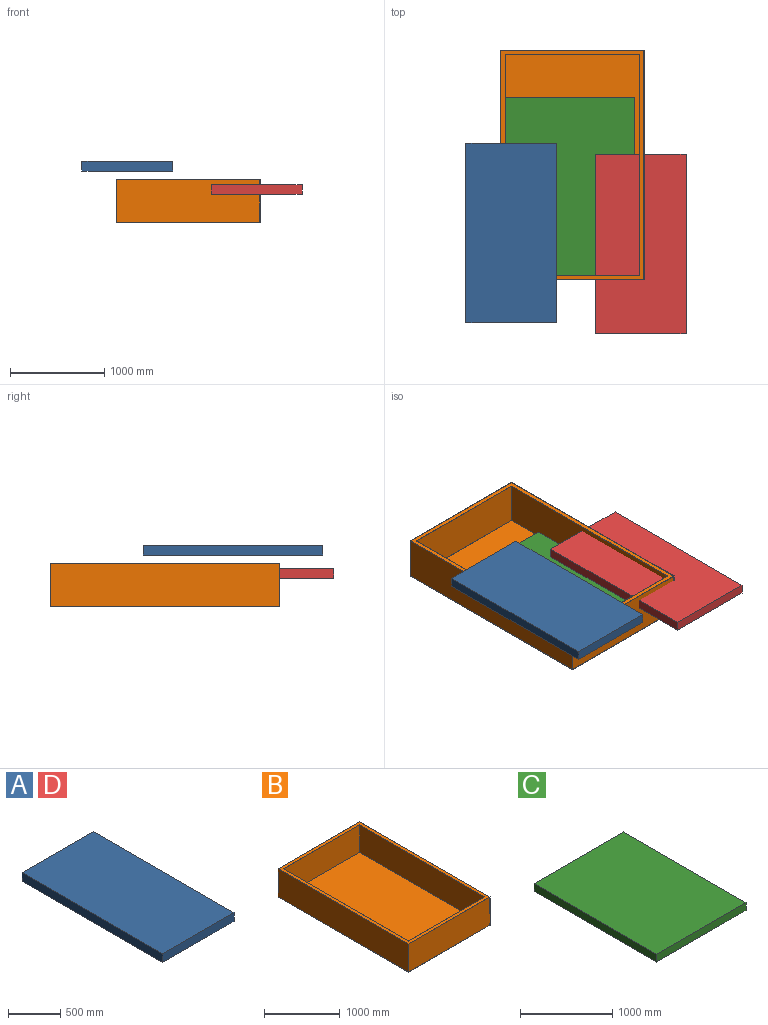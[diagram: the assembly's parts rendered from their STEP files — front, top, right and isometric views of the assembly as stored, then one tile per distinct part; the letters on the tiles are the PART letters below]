
ASSEMBLY  parts=4 mates=3
PART A: 6 faces, bbox 965.2x1905x101.6 mm
  f0: plane 1905x101.6mm, normal (-1,0,0), area 193548mm2, adj f1,f3,f4,f5
  f1: plane 965.2x101.6mm, normal (0,-1,0), area 98064.3mm2, adj f0,f2,f4,f5
  f2: plane 1905x101.6mm, normal (1,0,0), area 193548mm2, adj f1,f3,f4,f5
  f3: plane 965.2x101.6mm, normal (0,1,0), area 98064.3mm2, adj f0,f2,f4,f5
  f4: plane 1905x965.2mm, normal (0,0,1), area 1838706mm2, adj f0,f1,f2,f3
  f5: plane 1905x965.2mm, normal (0,0,-1), area 1838706mm2, adj f0,f1,f2,f3
PART B: 22 faces, bbox 1524x2438.4x457.2 mm
  f0: plane 2438.4x1524mm, normal (0,0,1), area 392257.3mm2, adj f1,f2,f3,f4,f6,f7,f8,f9
  f1: plane 2438.4x457.2mm, normal (-1,0,0), area 1114836.5mm2, adj f0,f2,f4,f5
  f2: plane 1524x457.2mm, normal (0,-1,0), area 696772.8mm2, adj f0,f1,f3,f5
  f3: plane 2438.4x457.2mm, normal (1,0,0), area 1114836.5mm2, adj f0,f2,f4,f5
  f4: plane 1524x457.2mm, normal (0,1,0), area 696772.8mm2, adj f0,f1,f3,f5
  f5: plane 2438.4x1524mm, normal (0,0,-1), area 3716121.6mm2, adj f1,f2,f3,f4
  f6: plane 1422.4x444.5mm, normal (0,-1,0), area 632256.8mm2, adj f0,f7,f9,f10
  f7: plane 2336.8x444.5mm, normal (1,0,0), area 1038707.6mm2, adj f0,f6,f8,f10
  f8: plane 1422.4x444.5mm, normal (0,1,0), area 632256.8mm2, adj f0,f7,f9,f10
  f9: plane 2336.8x444.5mm, normal (-1,0,0), area 1038707.6mm2, adj f0,f6,f8,f10
  f10: plane 2336.8x1422.4mm, normal (0,0,1), area 3323864.3mm2, adj f6,f7,f8,f9
  f11: plane 2433.32x1518.92mm, normal (0,0,-1), area 353031.6mm2, adj f12,f13,f14,f15,f17,f18,f19,f20
  f12: plane 2433.32x452.12mm, normal (1,0,0), area 1100152.6mm2, adj f11,f13,f15,f16
  f13: plane 1518.92x452.12mm, normal (0,1,0), area 686734.1mm2, adj f11,f12,f14,f16
  f14: plane 2433.32x452.12mm, normal (-1,0,0), area 1100152.6mm2, adj f11,f13,f15,f16
  f15: plane 1518.92x452.12mm, normal (0,-1,0), area 686734.1mm2, adj f11,f12,f14,f16
  f16: plane 2433.32x1518.92mm, normal (0,0,1), area 3696018.4mm2, adj f12,f13,f14,f15
  f17: plane 1427.48x444.5mm, normal (0,1,0), area 634514.9mm2, adj f11,f18,f20,f21
  f18: plane 2341.88x444.5mm, normal (-1,0,0), area 1040965.7mm2, adj f11,f17,f19,f21
  f19: plane 1427.48x444.5mm, normal (0,-1,0), area 634514.9mm2, adj f11,f18,f20,f21
  f20: plane 2341.88x444.5mm, normal (1,0,0), area 1040965.7mm2, adj f11,f17,f19,f21
  f21: plane 2341.88x1427.48mm, normal (0,0,-1), area 3342986.9mm2, adj f17,f18,f19,f20
PART C: 6 faces, bbox 1371.6x1879.6x101.6 mm
  f0: plane 1879.6x101.6mm, normal (-1,0,0), area 190967.4mm2, adj f1,f3,f4,f5
  f1: plane 1371.6x101.6mm, normal (0,-1,0), area 139354.6mm2, adj f0,f2,f4,f5
  f2: plane 1879.6x101.6mm, normal (1,0,0), area 190967.4mm2, adj f1,f3,f4,f5
  f3: plane 1371.6x101.6mm, normal (0,1,0), area 139354.6mm2, adj f0,f2,f4,f5
  f4: plane 1879.6x1371.6mm, normal (0,0,1), area 2578059.4mm2, adj f0,f1,f2,f3
  f5: plane 1879.6x1371.6mm, normal (0,0,-1), area 2578059.4mm2, adj f0,f1,f2,f3
PART D: same geometry as A
PLACE A t=(-1392.39,1500.04,2571.46)mm
PLACE B t=(-1025.56,1957.24,2025.36)mm fixed
PLACE C t=(-974.76,2008.04,2038.06)mm
PLACE D t=(-21.88,1382.54,2325.53)mm
MATE parallel B.f10 <-> C.f5  axis (0,0,1) through (-263.56,3176.44,2038.06)mm
MATE parallel C.f3 <-> B.f6  axis (0,1,0) through (-288.96,3887.64,2088.86)mm
MATE parallel A.f3 <-> D.f3  axis (0,1,0) through (-1392.39,3405.04,2673.06)mm
